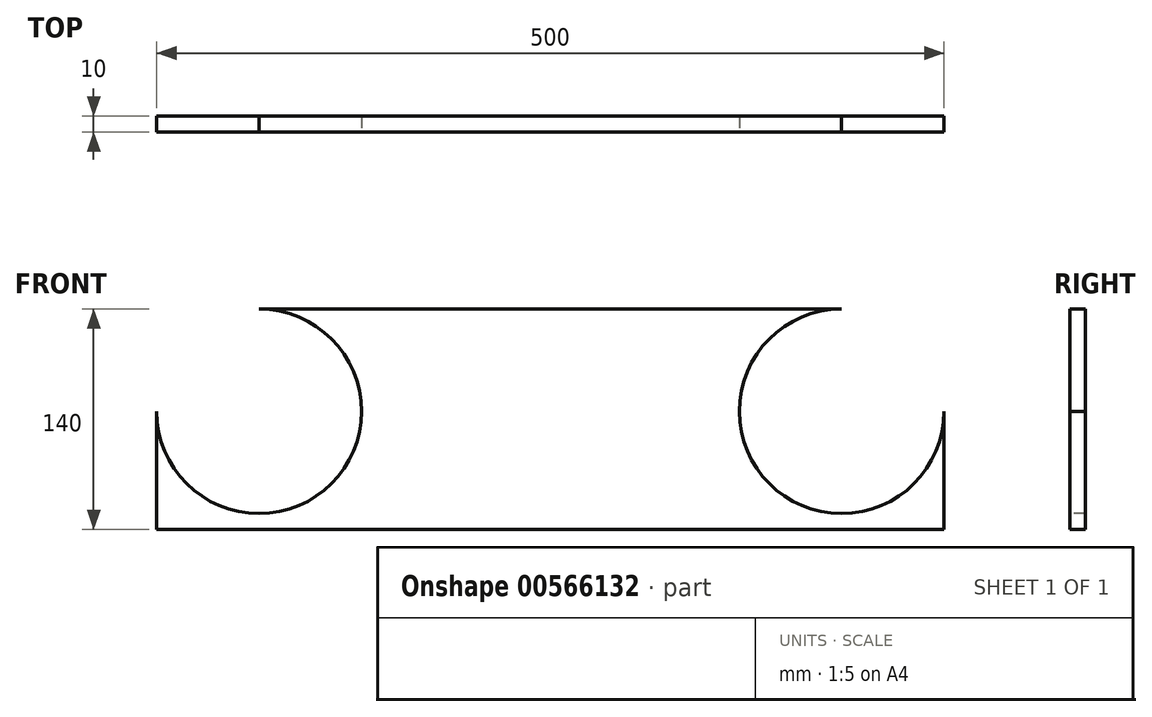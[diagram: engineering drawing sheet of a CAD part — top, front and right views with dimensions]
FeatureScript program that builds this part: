
annotation { "Feature Type Name" : "Feature", "Feature Type Description" : "" }
export const myFeature = defineFeature(function(context is Context, id is Id, definition is map)
    precondition{}
    {
        {
            var Q0;
            Q0=qCreatedBy(makeId("Front.planeOp"),FACE);
            var sketch = newSketch(context, id + "F0", { "sketchPlane" : qUnion([Q0])});
            skLineSegment(sketch, "E0.bottom", {"start": v(-185, 300) * mm, "end": v(185, 300) * mm});
            skLineSegment(sketch, "E0.left", {"start": v(-250, 235) * mm, "end": v(-250, 160) * mm});
            skLineSegment(sketch, "E0.right", {"start": v(250, 235) * mm, "end": v(250, 160) * mm});
            skPoint(sketch, "E0.middle", {"position": v(0, 0) * mm});
            skPoint(sketch, "E1.visualSharp", {"position": v(-250, 300) * mm});
            skArc(sketch, "E1.filletArc", {"start": v(-185, 300) * mm, "mid": v(-230.96, 280.96) * mm, "end": v(-250, 235) * mm});
            skPoint(sketch, "E2.visualSharp", {"position": v(250, 300) * mm});
            skArc(sketch, "E2.filletArc", {"start": v(250, 235) * mm, "mid": v(230.96, 280.96) * mm, "end": v(185, 300) * mm});
            skPoint(sketch, "E3.visualSharp", {"position": v(-250, -300) * mm});
            skPoint(sketch, "E4.visualSharp", {"position": v(250, -300) * mm});
            skCircle(sketch, "E5", {"center": v(-185, 235) * mm, "radius": 65 * mm});
            skCircle(sketch, "E6", {"center": v(185, 235) * mm, "radius": 65 * mm});
            skLineSegment(sketch, "E7", {"start": v(0, 300) * mm, "end": v(0, 160) * mm});
            skLineSegment(sketch, "E8", {"start": v(0, 160) * mm, "end": v(-250, 160) * mm});
            skLineSegment(sketch, "E9", {"start": v(0, 160) * mm, "end": v(250, 160) * mm});
            skSolve(sketch);
        }
        {
            var Q0;
            Q0 = qSketchRegion(id + "F0", true);
            extrude(context, id + "F1", {"entities" : qUnion([Q0]), "oppositeDirection" : true, "depth" : 10 * mm, "offsetDistance" : 25 * mm});
        }
        {
            var Q0;
            {var subQ0=sQuery(id+"F0.wireOp",EDGE,"E5");var subQ1=makeQuery(id+"F0.imprint","INTERSECT",VERTEX,{"derivedFrom":[sQuery(id+"F0.wireOp",EDGE,"E0.bottom"),subQ0]});Q0=makeQuery(id+"F0.imprint","IMPRINT",FACE,{"disambiguationData":[TD([[makeQuery(id+"F0.imprint","IMPRINT",EDGE,{"disambiguationData":[TD([[subQ1,-1.0]])],"derivedFrom":subQ0}),1.0]])]});}
            extrude(context, id + "F2", {"entities" : qUnion([Q0]), "operationType" : NewBodyOperationType.REMOVE, "oppositeDirection" : true, "depth" : 25 * mm, "offsetDistance" : 25 * mm});
        }
        {
            var Q0;
            {var subQ0=sQuery(id+"F0.wireOp",EDGE,"E6");var subQ1=makeQuery(id+"F0.imprint","INTERSECT",VERTEX,{"derivedFrom":[sQuery(id+"F0.wireOp",EDGE,"E0.bottom"),subQ0]});Q0=makeQuery(id+"F0.imprint","IMPRINT",FACE,{"disambiguationData":[TD([[makeQuery(id+"F0.imprint","IMPRINT",EDGE,{"disambiguationData":[TD([[subQ1,1.0]])],"derivedFrom":subQ0}),1.0]])]});}
            extrude(context, id + "F3", {"entities" : qUnion([Q0]), "operationType" : NewBodyOperationType.REMOVE, "oppositeDirection" : true, "depth" : 25 * mm, "offsetDistance" : 25 * mm});
        }
    });
